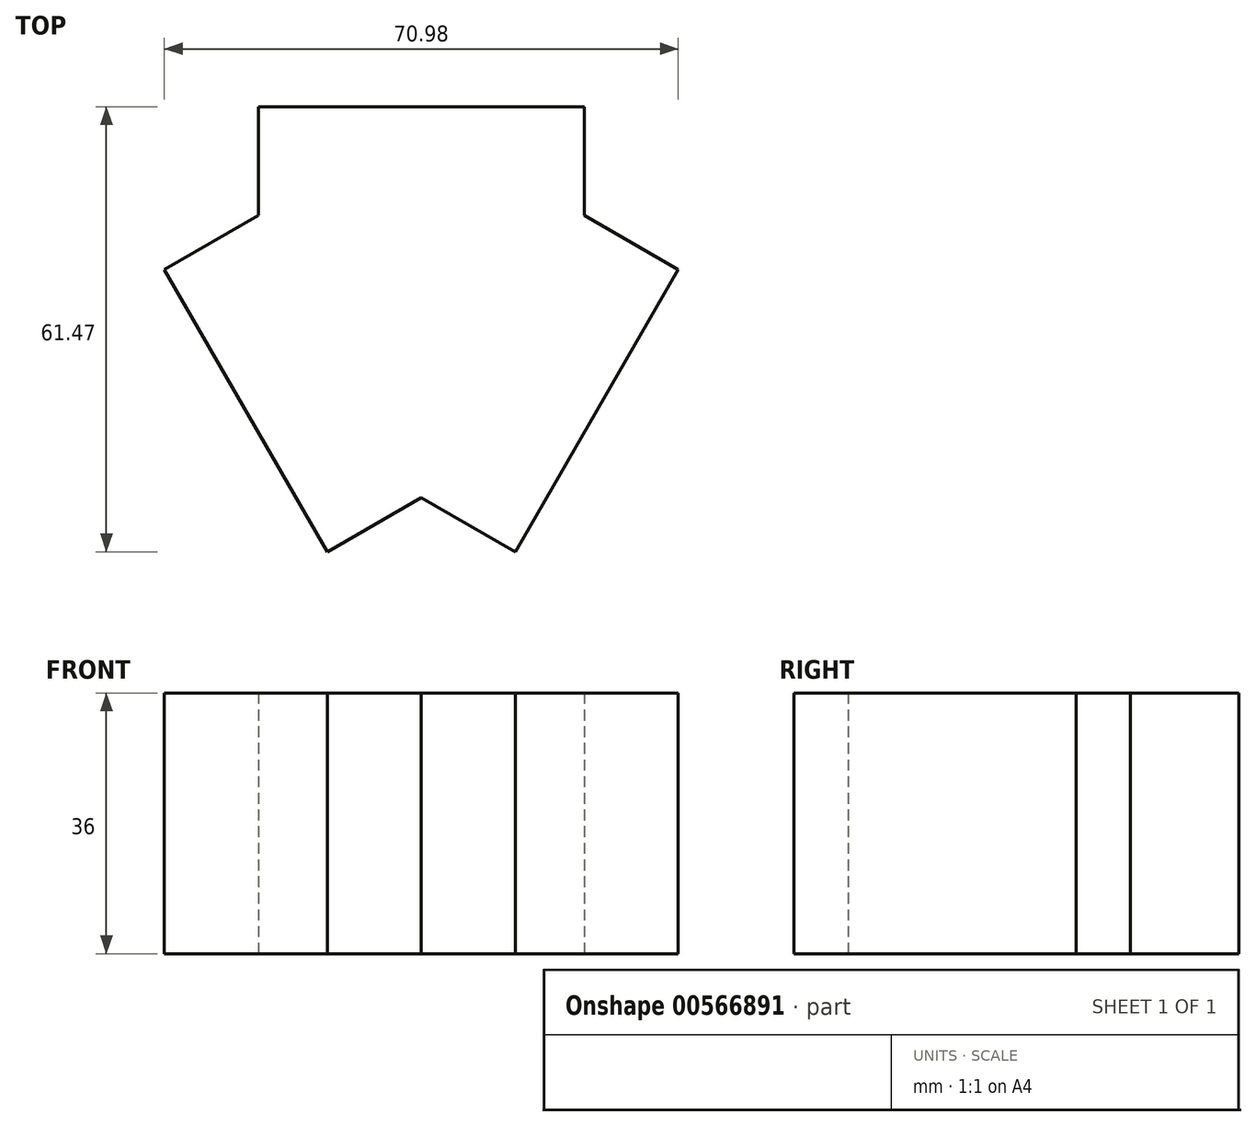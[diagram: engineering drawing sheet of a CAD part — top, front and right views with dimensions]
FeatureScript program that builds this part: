
annotation { "Feature Type Name" : "Feature", "Feature Type Description" : "" }
export const myFeature = defineFeature(function(context is Context, id is Id, definition is map)
    precondition{}
    {
        {
            var Q0;
            Q0=qCreatedBy(makeId("Top.planeOp"),FACE);
            var sketch = newSketch(context, id + "F0", { "sketchPlane" : qUnion([Q0])});
            skCircle(sketch, "E0.cCircle", {"center": v(0, 0) * mm, "radius": 13 * mm, "construction": true});
            skLineSegment(sketch, "E0.0", {"start": v(-22.5, 13) * mm, "end": v(22.5, 13) * mm});
            skLineSegment(sketch, "E0.1", {"start": v(22.5, 13) * mm, "end": v(0, -25.98) * mm});
            skLineSegment(sketch, "E0.2", {"start": v(0, -25.98) * mm, "end": v(-22.5, 13) * mm});
            skPoint(sketch, "E0.0.midPoint", {"position": v(0, 13) * mm});
            skSolve(sketch);
        }
        {
            var Q0;
            Q0=makeQuery(id+"F0.imprint","IMPRINT",FACE,{"disambiguationData":[TD([[makeQuery(id+"F0.imprint","IMPRINT",EDGE,{"derivedFrom":sQuery(id+"F0.wireOp",EDGE,"E0.0")}),-1.0]])]});
            extrude(context, id + "F1", {"entities" : qUnion([Q0]), "endBound" : BoundingType.SYMMETRIC, "depth" : 36 * mm, "offsetDistance" : 25 * mm});
        }
        {
            var Q0;
            Q0=makeQuery(id+"F1.opExtrude","SWEPT_FACE",FACE,{"disambiguationData":[OSD([sQuery(id+"F0.wireOp",EDGE,"E0.1")])]});
            extrude(context, id + "F2", {"entities" : qUnion([Q0]), "operationType" : NewBodyOperationType.ADD, "depth" : 15 * mm, "offsetDistance" : 25 * mm});
        }
        {
            var Q0;
            Q0=makeQuery(id+"F1.opExtrude","SWEPT_FACE",FACE,{"disambiguationData":[OSD([sQuery(id+"F0.wireOp",EDGE,"E0.0")])]});
            extrude(context, id + "F3", {"entities" : qUnion([Q0]), "operationType" : NewBodyOperationType.ADD, "depth" : 15 * mm, "offsetDistance" : 25 * mm});
        }
        {
            var Q0;
            Q0=makeQuery(id+"F1.opExtrude","SWEPT_FACE",FACE,{"disambiguationData":[OSD([sQuery(id+"F0.wireOp",EDGE,"E0.2")])]});
            extrude(context, id + "F4", {"entities" : qUnion([Q0]), "operationType" : NewBodyOperationType.ADD, "depth" : 15 * mm, "offsetDistance" : 25 * mm});
        }
        {
            var Q0;
            {var subQ0=sQuery(id+"F0.wireOp",EDGE,"E0.2");var subQ1=sQuery(id+"F0.wireOp",EDGE,"E0.1");var subQ2=makeQuery(id+"F1.opExtrude","CAP_VERTEX",VERTEX,{"disambiguationData":[OSD([subQ1,subQ0])],"isStart":true});var subQ3=makeQuery(id+"F2.boolean.opBoolean","MERGE",VERTEX,{"derivedFrom":[subQ2,makeQuery(id+"F2.opExtrude","CAP_VERTEX",VERTEX,{"disambiguationData":[OSD([subQ1,subQ0]),TDD([subQ2])],"isStart":true})]});Q0=makeQuery(id+"F4.boolean.opBoolean","MERGE",VERTEX,{"derivedFrom":[subQ3,makeQuery(id+"F4.opExtrude","CAP_VERTEX",VERTEX,{"disambiguationData":[OSD([subQ1,subQ0]),TDD([subQ3])],"isStart":true})]});}
            var Q1;
            {var subQ0=sQuery(id+"F0.wireOp",EDGE,"E0.2");var subQ1=sQuery(id+"F0.wireOp",EDGE,"E0.1");var subQ2=makeQuery(id+"F1.opExtrude","CAP_VERTEX",VERTEX,{"disambiguationData":[OSD([subQ1,subQ0])],"isStart":false});var subQ3=makeQuery(id+"F2.boolean.opBoolean","MERGE",VERTEX,{"derivedFrom":[subQ2,makeQuery(id+"F2.opExtrude","CAP_VERTEX",VERTEX,{"disambiguationData":[OSD([subQ1,subQ0]),TDD([subQ2])],"isStart":true})]});Q1=makeQuery(id+"F4.boolean.opBoolean","MERGE",VERTEX,{"derivedFrom":[subQ3,makeQuery(id+"F4.opExtrude","CAP_VERTEX",VERTEX,{"disambiguationData":[OSD([subQ1,subQ0]),TDD([subQ3])],"isStart":true})]});}
            var Q2;
            Q2=qCreatedBy(makeId("Origin.pointOp"),VERTEX);
            cPlane(context, id + "F5", {"entities" : qUnion([Q0, Q1, Q2]), "cplaneType" : CPlaneType.THREE_POINT, "offset" : 25 * mm, "width" : 150 * mm, "height" : 150 * mm});
        }
        {
            var Q0;
            Q0=qCreatedBy(id+"F5.planeOp",FACE);
            var sketch = newSketch(context, id + "F6", { "sketchPlane" : qUnion([Q0])});
            skArc(sketch, "E1", {"start": v(10, -12.5) * mm, "mid": v(11.6, -11.02) * mm, "end": v(13, -9.34) * mm});
            skArc(sketch, "E2", {"start": v(10, -9.08) * mm, "mid": v(12.6, -4.87) * mm, "end": v(13.5, 0) * mm});
            skLineSegment(sketch, "E3", {"start": v(13, -9.34) * mm, "end": v(13, -37.57) * mm});
            skLineSegment(sketch, "E4", {"start": v(0, 0) * mm, "end": v(13.5, 0) * mm});
            skLineSegment(sketch, "E5", {"start": v(10, -12.5) * mm, "end": v(10, -9.08) * mm});
            skSolve(sketch);
        }
        {
            var Q0;
            Q0=sQuery(id+"F6.wireOp",EDGE,"E3");
            var Q1;
            Q1=sQuery(id+"F6.wireOp",EDGE,"E1");
            var Q2;
            Q2=sQuery(id+"F6.wireOp",EDGE,"E5");
            var Q3;
            Q3=sQuery(id+"F6.wireOp",EDGE,"E2");
            var Q4;
            Q4=sQuery(id+"F6.wireOp",EDGE,"E4");
            revolve(context, id + "F7", {"bodyType" : ToolBodyType.SURFACE, "surfaceEntities" : qUnion([Q0, Q1, Q2, Q3]), "axis" : qUnion([Q4]), "revolveType" : RevolveType.FULL});
        }
    });
